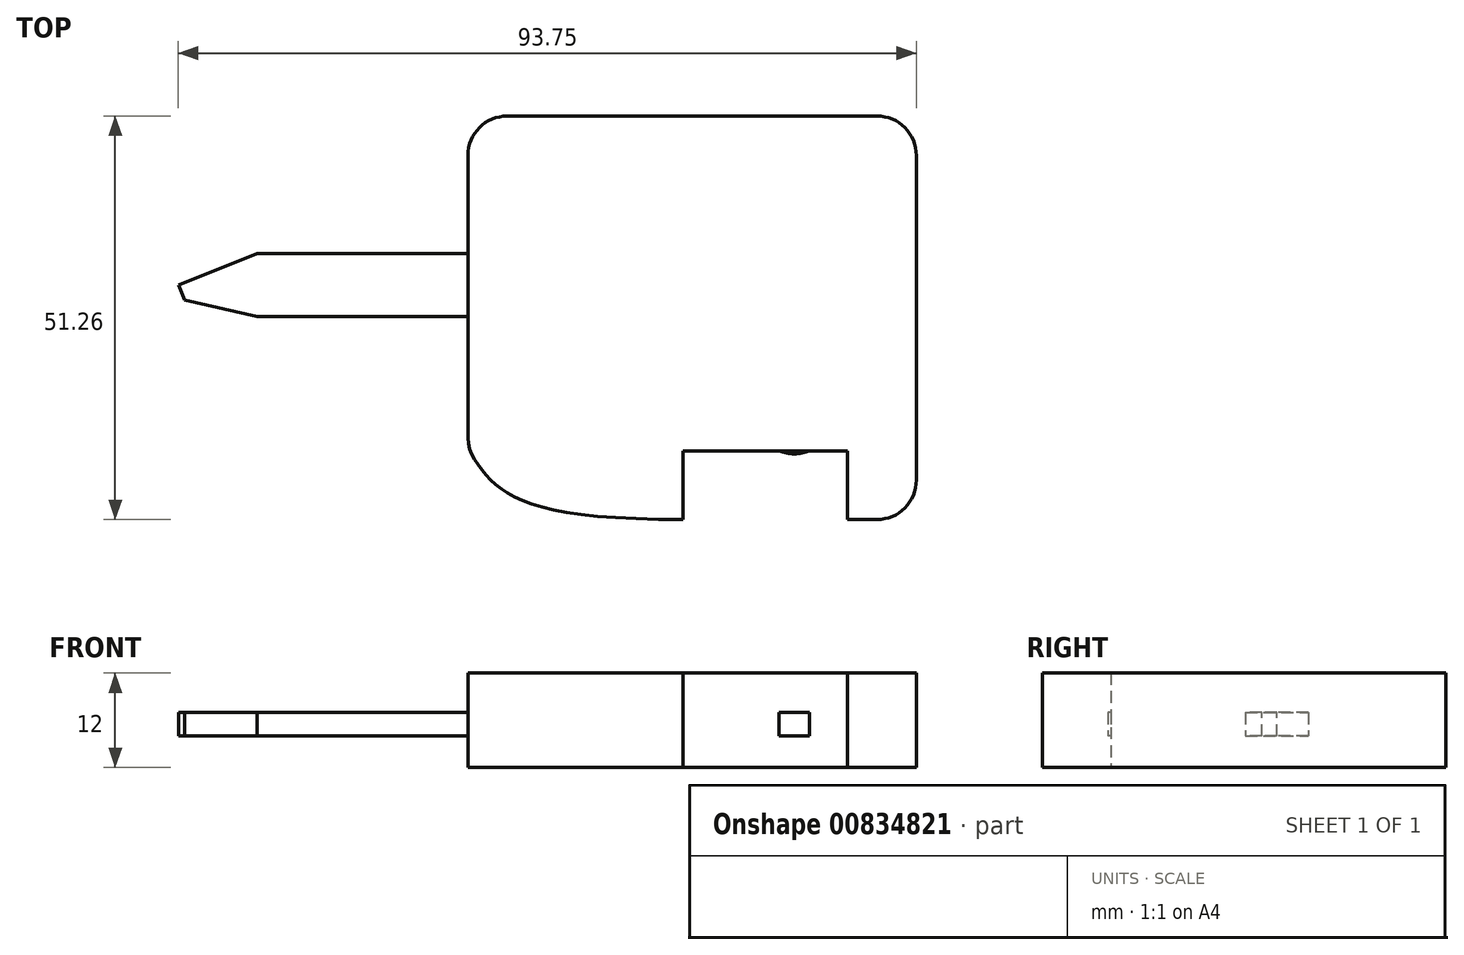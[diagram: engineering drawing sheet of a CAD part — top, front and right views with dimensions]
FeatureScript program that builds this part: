
annotation { "Feature Type Name" : "Feature", "Feature Type Description" : "" }
export const myFeature = defineFeature(function(context is Context, id is Id, definition is map)
    precondition{}
    {
        {
            var Q0;
            Q0=qCreatedBy(makeId("Top.planeOp"),FACE);
            var sketch = newSketch(context, id + "F0", { "sketchPlane" : qUnion([Q0])});
            skLineSegment(sketch, "E0.bottom", {"start": v(13.38, 4) * mm, "end": v(-13.38, 4) * mm});
            skLineSegment(sketch, "E0.top", {"start": v(13.38, -4) * mm, "end": v(-13.38, -4) * mm});
            skLineSegment(sketch, "E0.left", {"start": v(13.38, 4) * mm, "end": v(13.38, -4) * mm});
            skLineSegment(sketch, "E0.right", {"start": v(-13.38, 4) * mm, "end": v(-13.38, -4) * mm});
            skPoint(sketch, "E0.middle", {"position": v(0, 0) * mm});
            skLineSegment(sketch, "E1", {"start": v(13.38, 4) * mm, "end": v(52.86, 21.04) * mm});
            skLineSegment(sketch, "E2", {"start": v(52.86, -21.04) * mm, "end": v(13.38, -4) * mm});
            skPoint(sketch, "E3.visualSharp", {"position": v(59.84, 24.06) * mm});
            skArc(sketch, "E3.filletArc", {"start": v(59.84, 16.45) * mm, "mid": v(57.58, 20.63) * mm, "end": v(52.86, 21.04) * mm});
            skPoint(sketch, "E4.visualSharp", {"position": v(59.84, -24.06) * mm});
            skArc(sketch, "E4.filletArc", {"start": v(52.86, -21.04) * mm, "mid": v(57.58, -20.63) * mm, "end": v(59.84, -16.45) * mm});
            skFitSpline(sketch, "E5", {"points": [v(59.84, 16.45) * mm, v(62.72, 0) * mm, v(59.84, -16.45) * mm], "startDerivative": vector(8.63, -28.9) * mm, "endDerivative": vector(-8.63, -28.9) * mm});
            skLineSegment(sketch, "E6.bottom", {"start": v(56.36, 9.34) * mm, "end": v(53.96, 9.34) * mm});
            skLineSegment(sketch, "E6.top", {"start": v(56.36, -9.34) * mm, "end": v(53.96, -9.34) * mm});
            skLineSegment(sketch, "E6.left", {"start": v(56.36, 9.34) * mm, "end": v(56.36, -9.34) * mm});
            skLineSegment(sketch, "E6.right", {"start": v(53.96, 9.34) * mm, "end": v(53.96, -9.34) * mm});
            skPoint(sketch, "E6.middle", {"position": v(55.16, 0) * mm});
            skSolve(sketch);
        }
        {
            var Q0;
            Q0=makeQuery(id+"F0.imprint","IMPRINT",FACE,{"disambiguationData":[TD([[makeQuery(id+"F0.imprint","IMPRINT",EDGE,{"derivedFrom":sQuery(id+"F0.wireOp",EDGE,"E0.bottom")}),1.0]])]});
            var Q1;
            Q1=makeQuery(id+"F0.imprint","IMPRINT",FACE,{"disambiguationData":[TD([[makeQuery(id+"F0.imprint","IMPRINT",EDGE,{"derivedFrom":sQuery(id+"F0.wireOp",EDGE,"E0.left")}),1.0]])]});
            extrude(context, id + "F1", {"entities" : qUnion([Q0, Q1]), "depth" : 3 * mm, "offsetDistance" : 25 * mm});
        }
        {
            var Q0;
            Q0=makeQuery(id+"F1.opExtrude","CAP_FACE",FACE,{"disambiguationData":[OSD([sQuery(id+"F0.wireOp",EDGE,"E0.bottom"),sQuery(id+"F0.wireOp",EDGE,"E0.top"),sQuery(id+"F0.wireOp",EDGE,"E0.right"),sQuery(id+"F0.wireOp",EDGE,"E1"),sQuery(id+"F0.wireOp",EDGE,"E2"),sQuery(id+"F0.wireOp",EDGE,"E3.filletArc"),sQuery(id+"F0.wireOp",EDGE,"E4.filletArc"),sQuery(id+"F0.wireOp",EDGE,"E5"),sQuery(id+"F0.wireOp",EDGE,"E6.bottom"),sQuery(id+"F0.wireOp",EDGE,"E6.top"),sQuery(id+"F0.wireOp",EDGE,"E6.left"),sQuery(id+"F0.wireOp",EDGE,"E6.right")])],"isStart":false});
            var sketch = newSketch(context, id + "F2", { "sketchPlane" : qUnion([Q0])});
            skLineSegment(sketch, "E7", {"start": v(70.35, -24.79) * mm, "end": v(70.35, 16.47) * mm});
            skLineSegment(sketch, "E8", {"start": v(65.35, 21.47) * mm, "end": v(18.38, 21.47) * mm});
            skLineSegment(sketch, "E9", {"start": v(13.38, 16.47) * mm, "end": v(13.38, -19.45) * mm});
            skLineSegment(sketch, "E10.top", {"start": v(40.72, -21.06) * mm, "end": v(61.62, -21.06) * mm});
            skLineSegment(sketch, "E10.left", {"start": v(40.72, -29.79) * mm, "end": v(40.72, -21.06) * mm});
            skLineSegment(sketch, "E10.right", {"start": v(61.62, -29.79) * mm, "end": v(61.62, -21.06) * mm});
            skLineSegment(sketch, "E11", {"start": v(61.62, -29.79) * mm, "end": v(65.35, -29.79) * mm});
            skFitSpline(sketch, "E12", {"points": [v(13.38, -19.45) * mm, v(15.85, -24.29) * mm, v(40.72, -29.79) * mm], "startDerivative": vector(0, -15.29) * mm, "endDerivative": vector(75.62, 0) * mm});
            skPoint(sketch, "E13.visualSharp", {"position": v(13.38, 21.47) * mm});
            skArc(sketch, "E13.filletArc", {"start": v(18.38, 21.47) * mm, "mid": v(14.85, 20) * mm, "end": v(13.38, 16.47) * mm});
            skPoint(sketch, "E14.visualSharp", {"position": v(70.35, 21.47) * mm});
            skArc(sketch, "E14.filletArc", {"start": v(70.35, 16.47) * mm, "mid": v(68.88, 20) * mm, "end": v(65.35, 21.47) * mm});
            skPoint(sketch, "E15.visualSharp", {"position": v(70.35, -29.79) * mm});
            skArc(sketch, "E15.filletArc", {"start": v(65.35, -29.79) * mm, "mid": v(68.88, -28.32) * mm, "end": v(70.35, -24.79) * mm});
            skSolve(sketch);
        }
        {
            var Q0;
            Q0 = qSketchRegion(id + "F2", true);
            extrude(context, id + "F3", {"entities" : qUnion([Q0]), "operationType" : NewBodyOperationType.ADD, "depth" : 5 * mm, "offsetDistance" : 25 * mm, "hasSecondDirection" : true, "secondDirectionOppositeDirection" : true, "secondDirectionDepth" : 7 * mm});
        }
        {
            var Q0;
            {var subQ0=sQuery(id+"F0.wireOp",EDGE,"E0.bottom");var subQ1=sQuery(id+"F0.wireOp",EDGE,"E0.top");var subQ2=sQuery(id+"F0.wireOp",EDGE,"E0.right");Q0=makeQuery(id+"F3.boolean.opBoolean","SPLIT",FACE,{"disambiguationData":[TD([makeQuery(id+"F1.opExtrude","SWEPT_FACE",FACE,{"disambiguationData":[OSD([subQ0])]})])],"derivedFrom":makeQuery(id+"F1.opExtrude","CAP_FACE",FACE,{"disambiguationData":[OSD([subQ0,subQ1,subQ2,sQuery(id+"F0.wireOp",EDGE,"E1"),sQuery(id+"F0.wireOp",EDGE,"E2"),sQuery(id+"F0.wireOp",EDGE,"E3.filletArc"),sQuery(id+"F0.wireOp",EDGE,"E4.filletArc"),sQuery(id+"F0.wireOp",EDGE,"E5"),sQuery(id+"F0.wireOp",EDGE,"E6.bottom"),sQuery(id+"F0.wireOp",EDGE,"E6.top"),sQuery(id+"F0.wireOp",EDGE,"E6.left"),sQuery(id+"F0.wireOp",EDGE,"E6.right")])],"isStart":false})});}
            var sketch = newSketch(context, id + "F4", { "sketchPlane" : qUnion([Q0])});
            skLineSegment(sketch, "E16", {"start": v(-13.38, 4) * mm, "end": v(-23.4, 0) * mm});
            skPoint(sketch, "E16.endSnap0", {"position": v(-13.38, 0) * mm});
            skLineSegment(sketch, "E17", {"start": v(-23.4, 0) * mm, "end": v(-22.63, -1.93) * mm});
            skLineSegment(sketch, "E18", {"start": v(-22.63, -1.93) * mm, "end": v(-13.38, -4) * mm});
            skLineSegment(sketch, "E19", {"start": v(-13.38, -4) * mm, "end": v(-5.76, 0) * mm});
            skLineSegment(sketch, "E20", {"start": v(-5.76, 0) * mm, "end": v(-13.38, 4) * mm});
            skSolve(sketch);
        }
        {
            var Q0;
            Q0=makeQuery(id+"F4.imprint","IMPRINT",FACE,{"disambiguationData":[TD([[makeQuery(id+"F4.imprint","IMPRINT",EDGE,{"derivedFrom":sQuery(id+"F4.wireOp",EDGE,"E16")}),1.0]])]});
            var Q1;
            Q1=makeQuery(id+"F1.opExtrude","CAP_VERTEX",VERTEX,{"disambiguationData":[OSD([sQuery(id+"F0.wireOp",EDGE,"E0.bottom"),sQuery(id+"F0.wireOp",EDGE,"E0.right")])],"isStart":true});
            extrude(context, id + "F5", {"entities" : qUnion([Q0]), "operationType" : NewBodyOperationType.ADD, "endBound" : BoundingType.UP_TO_VERTEX, "oppositeDirection" : true, "depth" : 1.2 * mm, "endBoundEntityVertex" : qUnion([Q1]), "offsetDistance" : 25 * mm});
        }
    });
